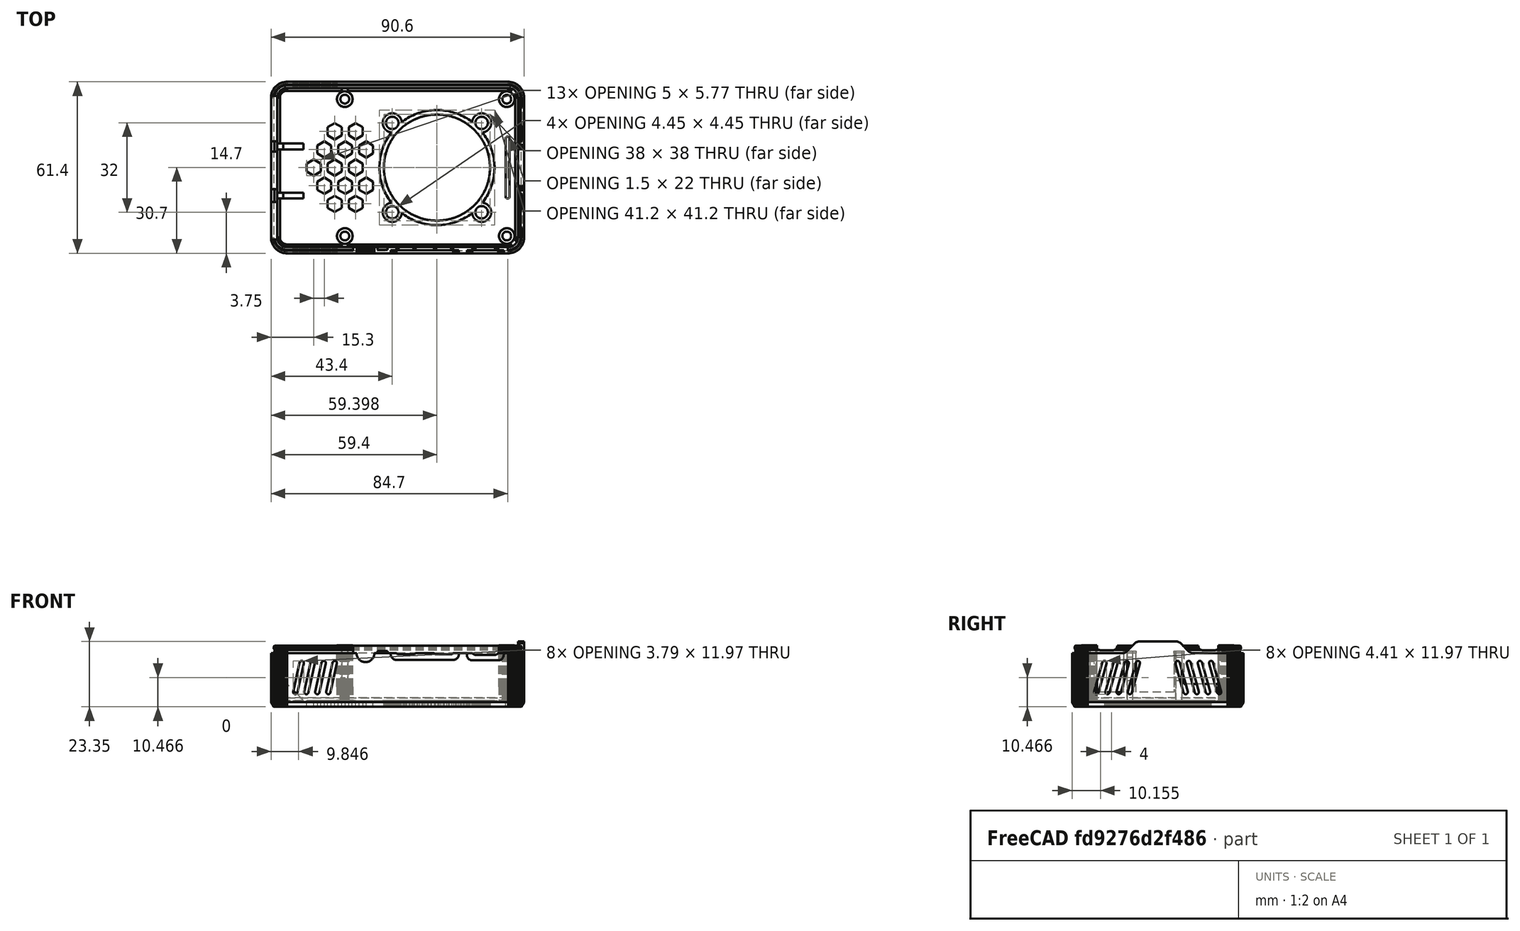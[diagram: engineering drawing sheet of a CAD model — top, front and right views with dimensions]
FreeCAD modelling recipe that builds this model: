
FCSTD DOCUMENT  (FreeCAD 1.2R20260217 (Git shallow))
Label: RemixRpi4Top
License: All rights reserved
LicenseURL: https://en.wikipedia.org/wiki/All_rights_reserved
objects: Part::Feature×2, Mesh::Feature×1, Part::Refine×1, App::Point×1, PartDesign::FeatureBase×1, Sketcher::SketchObject×1, PartDesign::Pocket×1, PartDesign::Body×1
note: 11 computed .brp shape members not serialized (recipe doc carries the construction recipe); baked Part::Feature solids carry a one-line shape summary decoded from their .brp

FEATURE [Mesh::Feature] Top_H20_Hex_SM_Fan40_Screws
FEATURE [Part::Feature] Top_H20_Hex_SM_Fan40_Screws001
  shape: bbox 90.6 x 61.4 x 23.35 mm, 41574 faces, 0 solids (baked)
FEATURE [Part::Refine] Top_H20_Hex_SM_Fan40_Screws002
  Source = -> Top_H20_Hex_SM_Fan40_Screws001
FEATURE [Part::Feature] Top_H20_Hex_SM_Fan40_Screws002_solid  label="Top_H20_Hex_SM_Fan40_Screws002 (Solid)"
  shape: bbox 90.6 x 61.4 x 23.35 mm, 15402 faces (baked)
FEATURE [App::Point] Origin001
  Role = Origin
FEATURE [PartDesign::FeatureBase] BaseFeature
  BaseFeature = -> Top_H20_Hex_SM_Fan40_Screws002_solid
  Suppressed = false
FEATURE [Sketcher::SketchObject] Sketch
  ArcFitTolerance = 1e-06
  AttachmentSupport = -> [BaseFeature]
  ExternalGeometry = -> [BaseFeature]
  ExternalTypes = [0]
  FullyConstrained = true
  MakeInternals = false
  MapMode = 5
  Placement = pos=(0,0,-23.7) rot=(1,0,0;3.14159rad)
  sketch-geometry (12):
    g0: LineSegment StartX=38.55 StartY=-17.5 StartZ=0 EndX=38.55 EndY=-38.5 EndZ=0
    g1: LineSegment StartX=39.05 StartY=-39 StartZ=0 EndX=39.55 EndY=-39 EndZ=0
    g2: LineSegment StartX=40.05 StartY=-38.5 StartZ=0 EndX=40.05 EndY=-17.5 EndZ=0
    g3: LineSegment StartX=39.55 StartY=-17 StartZ=0 EndX=39.05 EndY=-17 EndZ=0
    g4: ArcOfCircle CenterX=39.05 CenterY=-17.5 CenterZ=0 NormalX=0 NormalY=0 NormalZ=1 AngleXU=0 Radius=0.5 StartAngle=1.5708 EndAngle=3.14159
    g5: GeomPoint [constr] X=38.55 Y=-17 Z=0
    g6: ArcOfCircle CenterX=39.55 CenterY=-17.5 CenterZ=0 NormalX=0 NormalY=0 NormalZ=1 AngleXU=0 Radius=0.5 StartAngle=0 EndAngle=1.5708
    g7: GeomPoint [constr] X=40.05 Y=-17 Z=0
    g8: ArcOfCircle CenterX=39.55 CenterY=-38.5 CenterZ=0 NormalX=0 NormalY=0 NormalZ=1 AngleXU=0 Radius=0.5 StartAngle=4.71239 EndAngle=6.28319
    g9: GeomPoint [constr] X=40.05 Y=-39 Z=0
    g10: ArcOfCircle CenterX=39.05 CenterY=-38.5 CenterZ=0 NormalX=0 NormalY=0 NormalZ=1 AngleXU=0 Radius=0.5 StartAngle=3.14159 EndAngle=4.71239
    g11: GeomPoint [constr] X=38.55 Y=-39 Z=0
  constraints (28):
    c: Vertical(g0)
    c: Vertical(g2)
    c: Horizontal(g1)
    c: Horizontal(g3)
    c: DistanceX(g5,g7) = 1.5
    c: DistanceX(g7,g-3) = 5.15
    c: DistanceY(g9,g7) = 22
    c: DistanceY(g7,g-3) = 14
    c: PointOnObject(g5,g3)
    c: PointOnObject(g5,g0)
    c: Tangent(g3,g4) = -1.5708
    c: Tangent(g0,g4) = -1.5708
    c: PointOnObject(g7,g3)
    c: PointOnObject(g7,g2)
    c: Tangent(g3,g6) = -1.5708
    c: Tangent(g2,g6) = -1.5708
    c: PointOnObject(g9,g2)
    c: PointOnObject(g9,g1)
    c: Tangent(g2,g8) = -1.5708
    c: Tangent(g1,g8) = -1.5708
    c: PointOnObject(g11,g0)
    c: PointOnObject(g11,g1)
    c: Tangent(g0,g10) = -1.5708
    c: Tangent(g1,g10) = -1.5708
    c: Equal(g10,g8)
    c: Equal(g8,g6)
    c: Equal(g6,g4)
    c: Radius(g6) = 0.5
FEATURE [PartDesign::Pocket] Pocket
  BaseFeature = -> BaseFeature
  Direction = (0,0,1)
  Length = 5
  Length2 = 5
  Profile = -> Sketch
  ReferenceAxis = -> Sketch [N_Axis]
  Refine = true
  SideType = 0
  Suppressed = false
  Type = 0
  Type2 = 0
FEATURE [PartDesign::Body] Body
  AllowCompound = true
  BaseFeature = -> Top_H20_Hex_SM_Fan40_Screws002_solid
  Group = -> [BaseFeature,Sketch,Pocket]
  Origin = -> Origin
  Tip = -> Pocket
